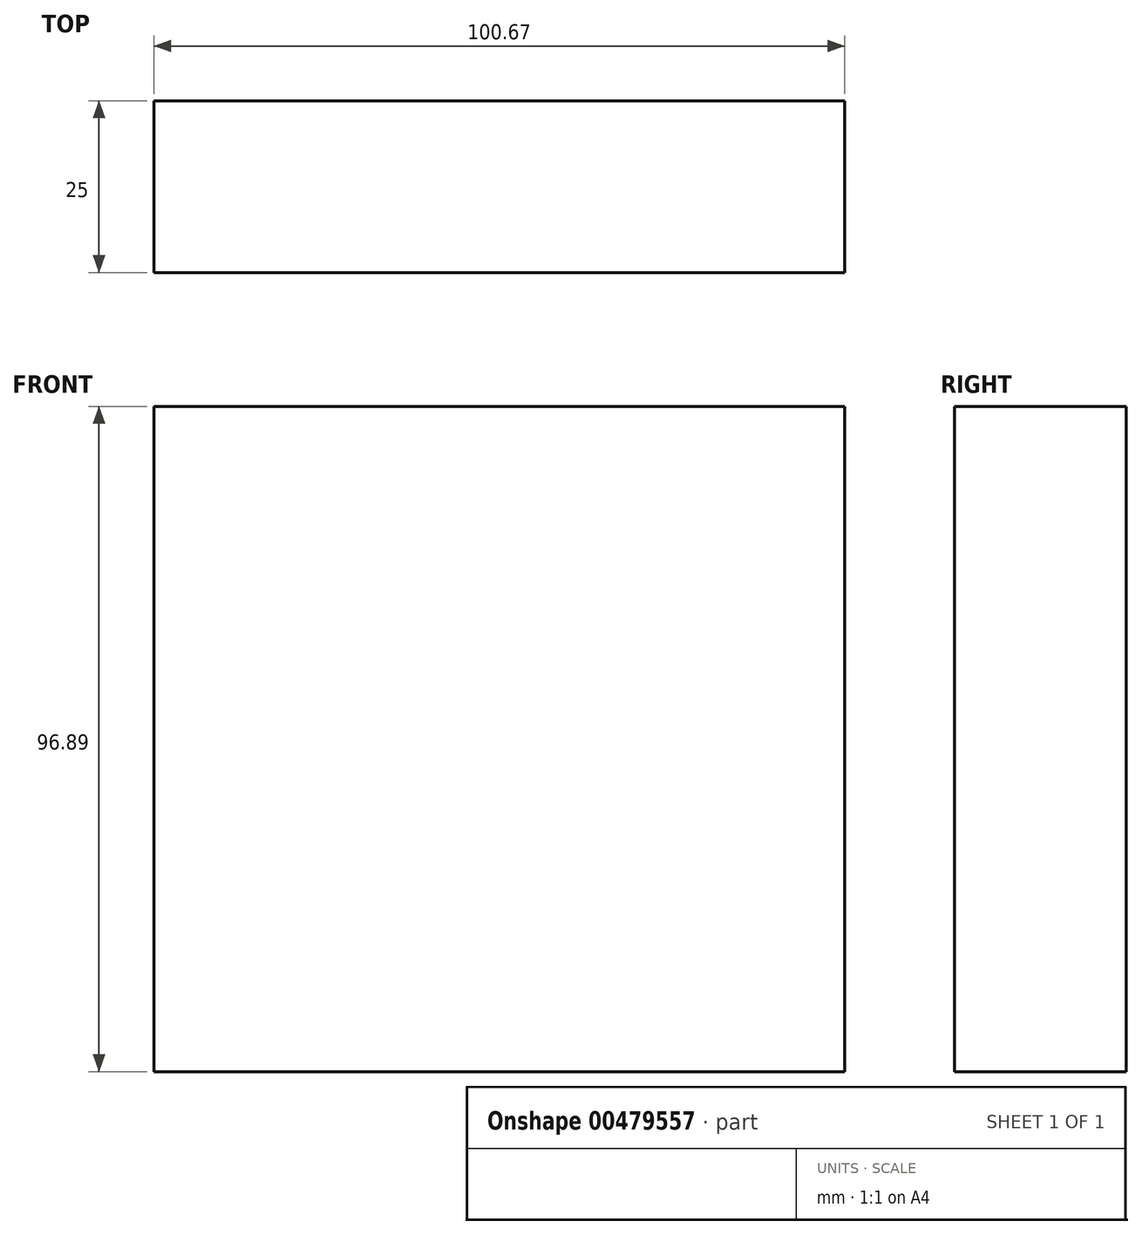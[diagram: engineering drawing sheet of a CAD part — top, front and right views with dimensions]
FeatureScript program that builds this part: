
annotation { "Feature Type Name" : "Feature", "Feature Type Description" : "" }
export const myFeature = defineFeature(function(context is Context, id is Id, definition is map)
    precondition{}
    {
        {
            var Q0;
            Q0=qCreatedBy(makeId("Front.planeOp"),FACE);
            var sketch = newSketch(context, id + "F0", { "sketchPlane" : qUnion([Q0])});
            skLineSegment(sketch, "E0.bottom", {"start": v(42.7, -55.2) * mm, "end": v(-57.98, -55.2) * mm});
            skLineSegment(sketch, "E0.top", {"start": v(42.7, 41.68) * mm, "end": v(-57.98, 41.68) * mm});
            skLineSegment(sketch, "E0.left", {"start": v(42.7, -55.2) * mm, "end": v(42.7, 41.68) * mm});
            skLineSegment(sketch, "E0.right", {"start": v(-57.98, -55.2) * mm, "end": v(-57.98, 41.68) * mm});
            skSolve(sketch);
        }
        {
            var Q0;
            Q0 = qSketchRegion(id + "F0", true);
            extrude(context, id + "F1", {"entities" : qUnion([Q0]), "depth" : 25 * mm});
        }
    });
